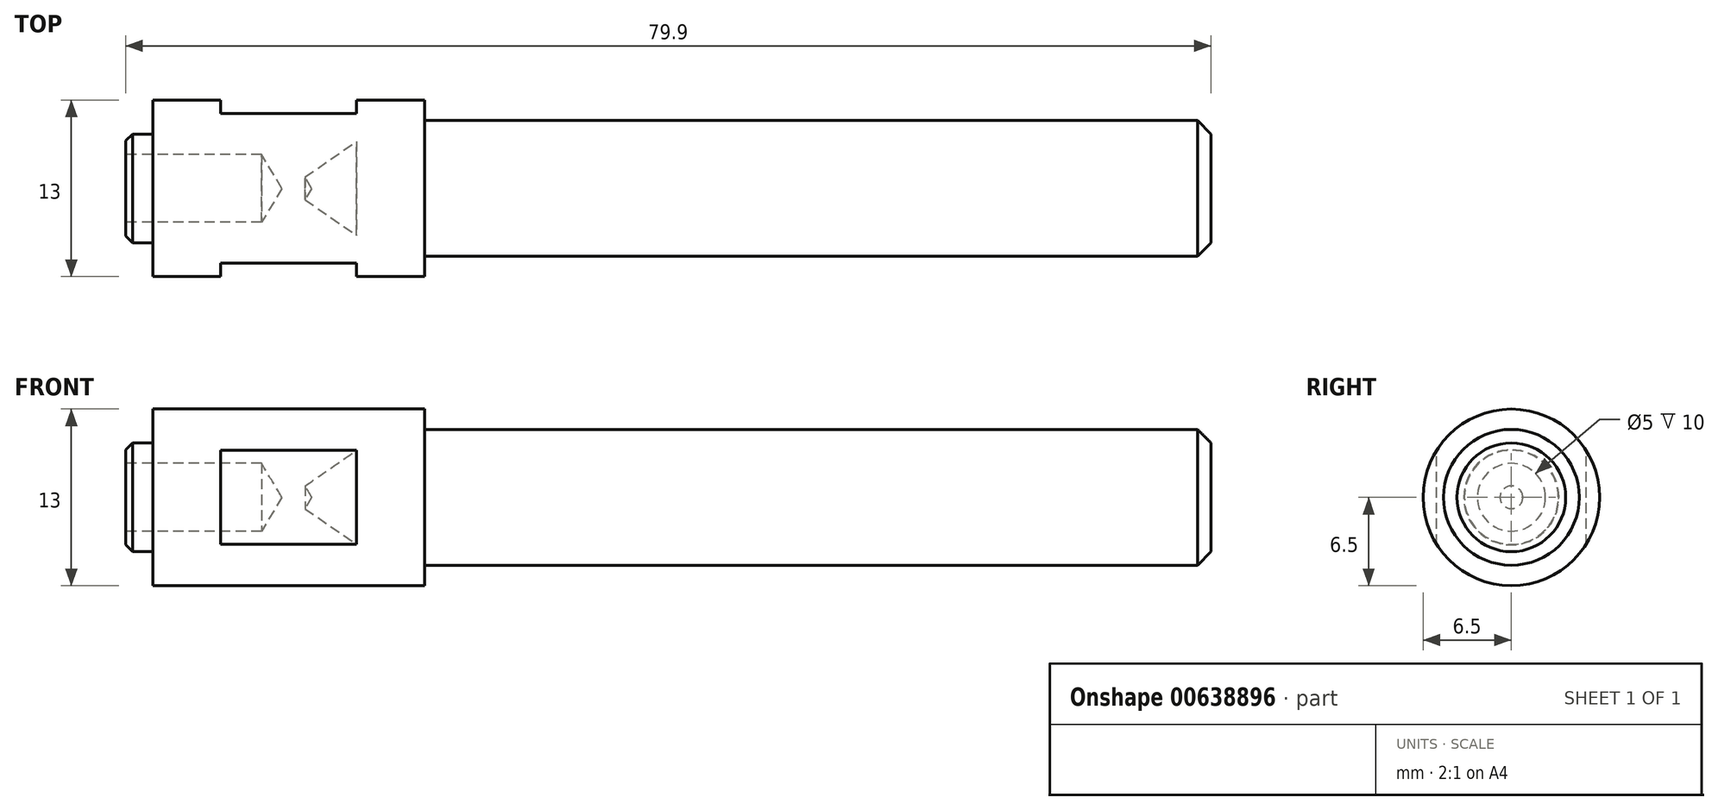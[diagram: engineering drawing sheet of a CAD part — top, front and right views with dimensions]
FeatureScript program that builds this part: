
annotation { "Feature Type Name" : "Feature", "Feature Type Description" : "" }
export const myFeature = defineFeature(function(context is Context, id is Id, definition is map)
    precondition{}
    {
        {
            var Q0;
            Q0=qCreatedBy(makeId("Front.planeOp"),FACE);
            var sketch = newSketch(context, id + "F0", { "sketchPlane" : qUnion([Q0])});
            skLineSegment(sketch, "E0", {"start": v(39.56, -3.46) * mm, "end": v(39.56, 3.46) * mm});
            skLineSegment(sketch, "E1", {"start": v(50.56, -3.46) * mm, "end": v(50.56, 3.46) * mm});
            skCircle(sketch, "E2", {"center": v(45.06, 0) * mm, "radius": 6.5 * mm});
            skLineSegment(sketch, "E3", {"start": v(38.06, 0) * mm, "end": v(52.06, 0) * mm});
            skLineSegment(sketch, "E4", {"start": v(45.06, -7) * mm, "end": v(45.06, 7) * mm});
            skCircle(sketch, "E5", {"center": v(45.06, 0) * mm, "radius": 5 * mm});
            skCircle(sketch, "E6", {"center": v(45.06, 0) * mm, "radius": 4 * mm});
            skLineSegment(sketch, "E7", {"start": v(-1, -5) * mm, "end": v(-57.9, -5) * mm});
            skLineSegment(sketch, "E8", {"start": v(-1, 5) * mm, "end": v(-57.9, 5) * mm});
            skLineSegment(sketch, "E9", {"start": v(-79.9, 0) * mm, "end": v(2, 0) * mm});
            skLineSegment(sketch, "E10", {"start": v(-79.9, -3.5) * mm, "end": v(-79.9, 3.5) * mm});
            skLineSegment(sketch, "E11", {"start": v(-79.4, -4) * mm, "end": v(-79.4, 4) * mm});
            skLineSegment(sketch, "E12", {"start": v(-57.9, -6.5) * mm, "end": v(-57.9, 6.5) * mm});
            skLineSegment(sketch, "E13", {"start": v(-79.9, 2.06) * mm, "end": v(-67.4, 2.06) * mm});
            skLineSegment(sketch, "E14", {"start": v(-67.4, 2.06) * mm, "end": v(-67.4, -2.07) * mm});
            skLineSegment(sketch, "E15", {"start": v(-67.4, -2.07) * mm, "end": v(-79.9, -2.07) * mm});
            skLineSegment(sketch, "E16", {"start": v(-67.4, -2.07) * mm, "end": v(-66.21, 0) * mm});
            skLineSegment(sketch, "E17", {"start": v(-67.4, 2.06) * mm, "end": v(-66.21, 0) * mm});
            skLineSegment(sketch, "E18", {"start": v(-69.9, 2.5) * mm, "end": v(-69.9, -2.5) * mm});
            skLineSegment(sketch, "E19", {"start": v(-69.9, -2.5) * mm, "end": v(-79.9, -2.5) * mm});
            skLineSegment(sketch, "E20", {"start": v(-79.9, 2.5) * mm, "end": v(-69.9, 2.5) * mm});
            skLineSegment(sketch, "E21", {"start": v(-69.9, -2.5) * mm, "end": v(-69.15, -2.07) * mm});
            skLineSegment(sketch, "E22", {"start": v(-69.9, 2.5) * mm, "end": v(-69.15, 2.06) * mm});
            skLineSegment(sketch, "E23", {"start": v(-64.84, 0) * mm, "end": v(-81.27, 0) * mm});
            skLineSegment(sketch, "E24", {"start": v(-79.4, -4) * mm, "end": v(-77.9, -4) * mm});
            skLineSegment(sketch, "E25", {"start": v(-79.4, 4) * mm, "end": v(-77.9, 4) * mm});
            skLineSegment(sketch, "E26", {"start": v(-77.9, -6.5) * mm, "end": v(-77.9, 6.5) * mm});
            skLineSegment(sketch, "E27", {"start": v(-62.9, -3.46) * mm, "end": v(-72.9, -3.46) * mm});
            skLineSegment(sketch, "E28", {"start": v(-72.9, -3.46) * mm, "end": v(-72.9, 3.46) * mm});
            skLineSegment(sketch, "E29", {"start": v(-62.9, -3.46) * mm, "end": v(-62.9, 3.46) * mm});
            skLineSegment(sketch, "E30", {"start": v(-62.9, 3.46) * mm, "end": v(-72.9, 3.46) * mm});
            skLineSegment(sketch, "E31", {"start": v(-72.9, -3.46) * mm, "end": v(-62.9, 3.46) * mm});
            skLineSegment(sketch, "E32", {"start": v(-72.9, 3.46) * mm, "end": v(-62.9, -3.46) * mm});
            skLineSegment(sketch, "E33", {"start": v(-77.9, 6.5) * mm, "end": v(-57.9, 6.5) * mm});
            skLineSegment(sketch, "E34", {"start": v(-77.9, -6.5) * mm, "end": v(-57.9, -6.5) * mm});
            skLineSegment(sketch, "E35", {"start": v(-79.4, 4) * mm, "end": v(-79.9, 3.5) * mm});
            skLineSegment(sketch, "E36", {"start": v(-79.9, -3.5) * mm, "end": v(-79.4, -4) * mm});
            skLineSegment(sketch, "E37", {"start": v(0, -4) * mm, "end": v(-1, -5) * mm});
            skLineSegment(sketch, "E38", {"start": v(0, 4) * mm, "end": v(-1, 5) * mm});
            skLineSegment(sketch, "E39", {"start": v(-1, 5) * mm, "end": v(-1, -5) * mm});
            skLineSegment(sketch, "E40.0", {"start": v(0, -4) * mm, "end": v(0, 4) * mm});
            skPoint(sketch, "E41", {"position": v(0, 0) * mm});
            skPoint(sketch, "E42.orphan", {"position": v(0, 6.5) * mm});
            skPoint(sketch, "E43.orphan", {"position": v(0, -6.5) * mm});
            skSolve(sketch);
        }
        {
            var Q0;
            {var subQ0=sQuery(id+"F0.wireOp",EDGE,"E8");Q0=makeQuery(id+"F0.imprint","IMPRINT",FACE,{"disambiguationData":[TD([[makeQuery(id+"F0.imprint","IMPRINT",EDGE,{"derivedFrom":subQ0}),1.0]])]});}
            var Q1;
            {var subQ5=sQuery(id+"F0.wireOp",EDGE,"E38");Q1=makeQuery(id+"F0.imprint","IMPRINT",FACE,{"disambiguationData":[TD([[makeQuery(id+"F0.imprint","IMPRINT",EDGE,{"derivedFrom":subQ5}),1.0]])]});}
            var Q2;
            {var subQ11=sQuery(id+"F0.wireOp",EDGE,"E30");Q2=makeQuery(id+"F0.imprint","IMPRINT",FACE,{"disambiguationData":[TD([[makeQuery(id+"F0.imprint","IMPRINT",EDGE,{"derivedFrom":subQ11}),-1.0]])]});}
            var Q3;
            {var subQ0=sQuery(id+"F0.wireOp",EDGE,"E25");Q3=makeQuery(id+"F0.imprint","IMPRINT",FACE,{"disambiguationData":[TD([[makeQuery(id+"F0.imprint","IMPRINT",EDGE,{"derivedFrom":subQ0}),-1.0]])]});}
            var Q4;
            {var subQ1=sQuery(id+"F0.wireOp",EDGE,"E13");var subQ10=makeQuery(id+"F0.imprint","INTERSECT",VERTEX,{"derivedFrom":[subQ1,sQuery(id+"F0.wireOp",EDGE,"E22")]});Q4=makeQuery(id+"F0.imprint","IMPRINT",FACE,{"disambiguationData":[TD([[makeQuery(id+"F0.imprint","IMPRINT",EDGE,{"disambiguationData":[TD([[subQ10,1.0]])],"derivedFrom":subQ1}),-1.0]])]});}
            var Q5;
            {var subQ0=sQuery(id+"F0.wireOp",EDGE,"E32");var subQ1=sQuery(id+"F0.wireOp",EDGE,"E13");var subQ2=makeQuery(id+"F0.imprint","INTERSECT",VERTEX,{"derivedFrom":[subQ1,subQ0]});Q5=makeQuery(id+"F0.imprint","IMPRINT",FACE,{"disambiguationData":[TD([[makeQuery(id+"F0.imprint","IMPRINT",EDGE,{"disambiguationData":[TD([[subQ2,-1.0]])],"derivedFrom":subQ1}),-1.0]])]});}
            var Q6;
            {var subQ0=sQuery(id+"F0.wireOp",EDGE,"E13");var subQ1=sQuery(id+"F0.wireOp",EDGE,"E11");var subQ2=makeQuery(id+"F0.imprint","INTERSECT",VERTEX,{"derivedFrom":[subQ1,subQ0]});Q6=makeQuery(id+"F0.imprint","IMPRINT",FACE,{"disambiguationData":[TD([[makeQuery(id+"F0.imprint","IMPRINT",EDGE,{"disambiguationData":[TD([[subQ2,-1.0]])],"derivedFrom":subQ1}),-1.0]])]});}
            var Q7;
            {var subQ0=sQuery(id+"F0.wireOp",EDGE,"E22");Q7=makeQuery(id+"F0.imprint","IMPRINT",FACE,{"disambiguationData":[TD([[makeQuery(id+"F0.imprint","IMPRINT",EDGE,{"derivedFrom":subQ0}),1.0]])]});}
            var Q8;
            {var subQ0=sQuery(id+"F0.wireOp",EDGE,"E26");var subQ1=sQuery(id+"F0.wireOp",EDGE,"E13");var subQ2=makeQuery(id+"F0.imprint","INTERSECT",VERTEX,{"derivedFrom":[subQ1,subQ0]});Q8=makeQuery(id+"F0.imprint","IMPRINT",FACE,{"disambiguationData":[TD([[makeQuery(id+"F0.imprint","IMPRINT",EDGE,{"disambiguationData":[TD([[subQ2,-1.0]])],"derivedFrom":subQ1}),1.0]])]});}
            var Q9;
            {var subQ0=sQuery(id+"F0.wireOp",EDGE,"E23");var subQ1=sQuery(id+"F0.wireOp",EDGE,"E11");var subQ2=makeQuery(id+"F0.imprint","INTERSECT",VERTEX,{"derivedFrom":[subQ1,subQ0]});Q9=makeQuery(id+"F0.imprint","IMPRINT",FACE,{"disambiguationData":[TD([[makeQuery(id+"F0.imprint","IMPRINT",EDGE,{"disambiguationData":[TD([[subQ2,-1.0]])],"derivedFrom":subQ1}),-1.0]])]});}
            var Q10;
            {var subQ0=sQuery(id+"F0.wireOp",EDGE,"E32");var subQ1=sQuery(id+"F0.wireOp",EDGE,"E18");var subQ2=makeQuery(id+"F0.imprint","INTERSECT",VERTEX,{"derivedFrom":[subQ1,subQ0]});Q10=makeQuery(id+"F0.imprint","IMPRINT",FACE,{"disambiguationData":[TD([[makeQuery(id+"F0.imprint","IMPRINT",EDGE,{"disambiguationData":[TD([[subQ2,-1.0]])],"derivedFrom":subQ1}),1.0]])]});}
            var Q11;
            {var subQ1=sQuery(id+"F0.wireOp",EDGE,"E14");var subQ3=sQuery(id+"F0.wireOp",EDGE,"E31");var subQ4=makeQuery(id+"F0.imprint","INTERSECT",VERTEX,{"derivedFrom":[subQ1,subQ3]});Q11=makeQuery(id+"F0.imprint","IMPRINT",FACE,{"disambiguationData":[TD([[makeQuery(id+"F0.imprint","IMPRINT",EDGE,{"disambiguationData":[TD([[subQ4,-1.0]])],"derivedFrom":subQ3}),1.0]])]});}
            var Q12;
            {var subQ0=sQuery(id+"F0.wireOp",EDGE,"E13");var subQ1=sQuery(id+"F0.wireOp",EDGE,"E10");var subQ2=makeQuery(id+"F0.imprint","INTERSECT",VERTEX,{"derivedFrom":[subQ1,subQ0]});Q12=makeQuery(id+"F0.imprint","IMPRINT",FACE,{"disambiguationData":[TD([[makeQuery(id+"F0.imprint","IMPRINT",EDGE,{"disambiguationData":[TD([[subQ2,1.0]])],"derivedFrom":subQ1}),-1.0]])]});}
            var Q13;
            {var subQ0=sQuery(id+"F0.wireOp",EDGE,"E28");var subQ1=sQuery(id+"F0.wireOp",EDGE,"E13");var subQ2=makeQuery(id+"F0.imprint","INTERSECT",VERTEX,{"derivedFrom":[subQ1,subQ0]});Q13=makeQuery(id+"F0.imprint","IMPRINT",FACE,{"disambiguationData":[TD([[makeQuery(id+"F0.imprint","IMPRINT",EDGE,{"disambiguationData":[TD([[subQ2,-1.0]])],"derivedFrom":subQ1}),1.0]])]});}
            var Q14;
            {var subQ0=sQuery(id+"F0.wireOp",EDGE,"E35");Q14=makeQuery(id+"F0.imprint","IMPRINT",FACE,{"disambiguationData":[TD([[makeQuery(id+"F0.imprint","IMPRINT",EDGE,{"derivedFrom":subQ0}),1.0]])]});}
            var Q15;
            {var subQ0=sQuery(id+"F0.wireOp",EDGE,"E32");var subQ1=sQuery(id+"F0.wireOp",EDGE,"E13");var subQ2=makeQuery(id+"F0.imprint","INTERSECT",VERTEX,{"derivedFrom":[subQ1,subQ0]});Q15=makeQuery(id+"F0.imprint","IMPRINT",FACE,{"disambiguationData":[TD([[makeQuery(id+"F0.imprint","IMPRINT",EDGE,{"disambiguationData":[TD([[subQ2,-1.0]])],"derivedFrom":subQ1}),1.0]])]});}
            var Q16;
            {var subQ0=sQuery(id+"F0.wireOp",EDGE,"E28");var subQ1=sQuery(id+"F0.wireOp",EDGE,"E13");var subQ2=makeQuery(id+"F0.imprint","INTERSECT",VERTEX,{"derivedFrom":[subQ1,subQ0]});Q16=makeQuery(id+"F0.imprint","IMPRINT",FACE,{"disambiguationData":[TD([[makeQuery(id+"F0.imprint","IMPRINT",EDGE,{"disambiguationData":[TD([[subQ2,-1.0]])],"derivedFrom":subQ1}),-1.0]])]});}
            var Q17;
            {var subQ0=sQuery(id+"F0.wireOp",EDGE,"E28");var subQ1=sQuery(id+"F0.wireOp",EDGE,"E20");var subQ2=makeQuery(id+"F0.imprint","INTERSECT",VERTEX,{"derivedFrom":[subQ1,subQ0]});Q17=makeQuery(id+"F0.imprint","IMPRINT",FACE,{"disambiguationData":[TD([[makeQuery(id+"F0.imprint","IMPRINT",EDGE,{"disambiguationData":[TD([[subQ2,-1.0]])],"derivedFrom":subQ1}),1.0]])]});}
            var Q18;
            {var subQ3=sQuery(id+"F0.wireOp",EDGE,"E9");var subQ5=sQuery(id+"F0.wireOp",EDGE,"E23");var subQ9=makeQuery(id+"F0.imprint","INTERSECT",VERTEX,{"derivedFrom":[subQ3,subQ5]});Q18=makeQuery(id+"F0.imprint","IMPRINT",FACE,{"disambiguationData":[TD([[makeQuery(id+"F0.imprint","IMPRINT",EDGE,{"disambiguationData":[TD([[subQ9,-1.0]])],"derivedFrom":subQ3}),1.0]])]});}
            var Q19;
            {var subQ0=sQuery(id+"F0.wireOp",EDGE,"E26");var subQ1=sQuery(id+"F0.wireOp",EDGE,"E13");var subQ2=makeQuery(id+"F0.imprint","INTERSECT",VERTEX,{"derivedFrom":[subQ1,subQ0]});Q19=makeQuery(id+"F0.imprint","IMPRINT",FACE,{"disambiguationData":[TD([[makeQuery(id+"F0.imprint","IMPRINT",EDGE,{"disambiguationData":[TD([[subQ2,-1.0]])],"derivedFrom":subQ1}),-1.0]])]});}
            var Q20;
            {var subQ0=sQuery(id+"F0.wireOp",EDGE,"E22");Q20=makeQuery(id+"F0.imprint","IMPRINT",FACE,{"disambiguationData":[TD([[makeQuery(id+"F0.imprint","IMPRINT",EDGE,{"derivedFrom":subQ0}),-1.0]])]});}
            var Q21;
            {var subQ0=sQuery(id+"F0.wireOp",EDGE,"E13");var subQ1=sQuery(id+"F0.wireOp",EDGE,"E10");var subQ2=makeQuery(id+"F0.imprint","INTERSECT",VERTEX,{"derivedFrom":[subQ1,subQ0]});Q21=makeQuery(id+"F0.imprint","IMPRINT",FACE,{"disambiguationData":[TD([[makeQuery(id+"F0.imprint","IMPRINT",EDGE,{"disambiguationData":[TD([[subQ2,-1.0]])],"derivedFrom":subQ1}),-1.0]])]});}
            var Q22;
            {var subQ0=sQuery(id+"F0.wireOp",EDGE,"E31");var subQ1=sQuery(id+"F0.wireOp",EDGE,"E14");var subQ2=makeQuery(id+"F0.imprint","INTERSECT",VERTEX,{"derivedFrom":[subQ1,subQ0]});Q22=makeQuery(id+"F0.imprint","IMPRINT",FACE,{"disambiguationData":[TD([[makeQuery(id+"F0.imprint","IMPRINT",EDGE,{"disambiguationData":[TD([[subQ2,-1.0]])],"derivedFrom":subQ1}),-1.0]])]});}
            var Q23;
            {var subQ0=sQuery(id+"F0.wireOp",EDGE,"E31");var subQ1=sQuery(id+"F0.wireOp",EDGE,"E14");var subQ2=makeQuery(id+"F0.imprint","INTERSECT",VERTEX,{"derivedFrom":[subQ1,subQ0]});Q23=makeQuery(id+"F0.imprint","IMPRINT",FACE,{"disambiguationData":[TD([[makeQuery(id+"F0.imprint","IMPRINT",EDGE,{"disambiguationData":[TD([[subQ2,-1.0]])],"derivedFrom":subQ1}),1.0]])]});}
            var Q24;
            Q24=sQuery(id+"F0.wireOp",EDGE,"E9");
            revolve(context, id + "F1", {"entities" : qUnion([Q0, Q1, Q2, Q3, Q4, Q5, Q6, Q7, Q8, Q9, Q10, Q11, Q12, Q13, Q14, Q15, Q16, Q17, Q18, Q19, Q20, Q21, Q22, Q23]), "axis" : qUnion([Q24]), "revolveType" : RevolveType.FULL});
        }
        {
            var Q0;
            Q0=makeQuery(id+"F1.opRevolve","SWEPT_FACE",FACE,{"disambiguationData":[OSD([sQuery(id+"F0.wireOp",EDGE,"E10")])]});
            var sketch = newSketch(context, id + "F2", { "sketchPlane" : qUnion([Q0])});
            skPoint(sketch, "E44", {"position": v(0, 0) * mm});
            skSolve(sketch);
        }
        {
            var Q0;
            Q0=sQuery(id+"F2.wireOp",VERTEX,"E44");
            var Q1;
            Q1=makeQuery(id+"F1.opRevolve","SWEPT_BODY",BODY,{"disambiguationData":[OSD([sQuery(id+"F0.wireOp",EDGE,"E8"),sQuery(id+"F0.wireOp",EDGE,"E9"),sQuery(id+"F0.wireOp",EDGE,"E10"),sQuery(id+"F0.wireOp",EDGE,"E12"),sQuery(id+"F0.wireOp",EDGE,"E23"),sQuery(id+"F0.wireOp",EDGE,"E25"),sQuery(id+"F0.wireOp",EDGE,"E26"),sQuery(id+"F0.wireOp",EDGE,"E33"),sQuery(id+"F0.wireOp",EDGE,"E35"),sQuery(id+"F0.wireOp",EDGE,"E38"),sQuery(id+"F0.wireOp",EDGE,"792cef95-4536-4853-a092-e6b57c81706a")])]});
            hole(context, id + "F3", {"style" : HoleStyle.SIMPLE, "endStyle" : HoleEndStyle.BLIND, "holeDiameter" : 5 * mm, "majorDiameter" : 5 * mm, "holeDepth" : 10 * mm, "isTappedThrough" : true, "tappedDepth" : 12 * mm, "tapClearance" : 3, "locations" : qUnion([Q0]), "scope" : qUnion([Q1])});
        }
        {
            var Q0;
            Q0=qCreatedBy(makeId("Top.planeOp"),FACE);
            var sketch = newSketch(context, id + "F4", { "sketchPlane" : qUnion([Q0])});
            skLineSegment(sketch, "E45.bottom", {"start": v(-72.9, 5.5) * mm, "end": v(-62.9, 5.5) * mm});
            skLineSegment(sketch, "E45.top", {"start": v(-72.9, 18.23) * mm, "end": v(-62.9, 18.23) * mm});
            skLineSegment(sketch, "E45.left", {"start": v(-72.9, 5.5) * mm, "end": v(-72.9, 18.23) * mm});
            skLineSegment(sketch, "E45.right", {"start": v(-62.9, 5.5) * mm, "end": v(-62.9, 18.23) * mm});
            skLineSegment(sketch, "E46.MirrorCS", {"start": v(-72.9, -5.5) * mm, "end": v(-62.9, -5.5) * mm});
            skLineSegment(sketch, "E47.MirrorCS", {"start": v(-62.9, -5.5) * mm, "end": v(-62.9, -18.23) * mm});
            skLineSegment(sketch, "E48.MirrorCS", {"start": v(-72.9, -5.5) * mm, "end": v(-72.9, -18.23) * mm});
            skLineSegment(sketch, "E49.MirrorCS", {"start": v(-72.9, -18.23) * mm, "end": v(-60.9, -18.23) * mm});
            skPoint(sketch, "E50.orphan", {"position": v(-72.9, 7.86) * mm});
            skPoint(sketch, "E51.orphan", {"position": v(-72.9, -7.86) * mm});
            skSolve(sketch);
        }
        {
            var Q0;
            Q0 = qSketchRegion(id + "F4", true);
            extrude(context, id + "F5", {"entities" : qUnion([Q0]), "operationType" : NewBodyOperationType.REMOVE, "endBound" : BoundingType.SYMMETRIC, "oppositeDirection" : true, "depth" : 25 * mm, "offsetDistance" : 25 * mm});
        }
    });
